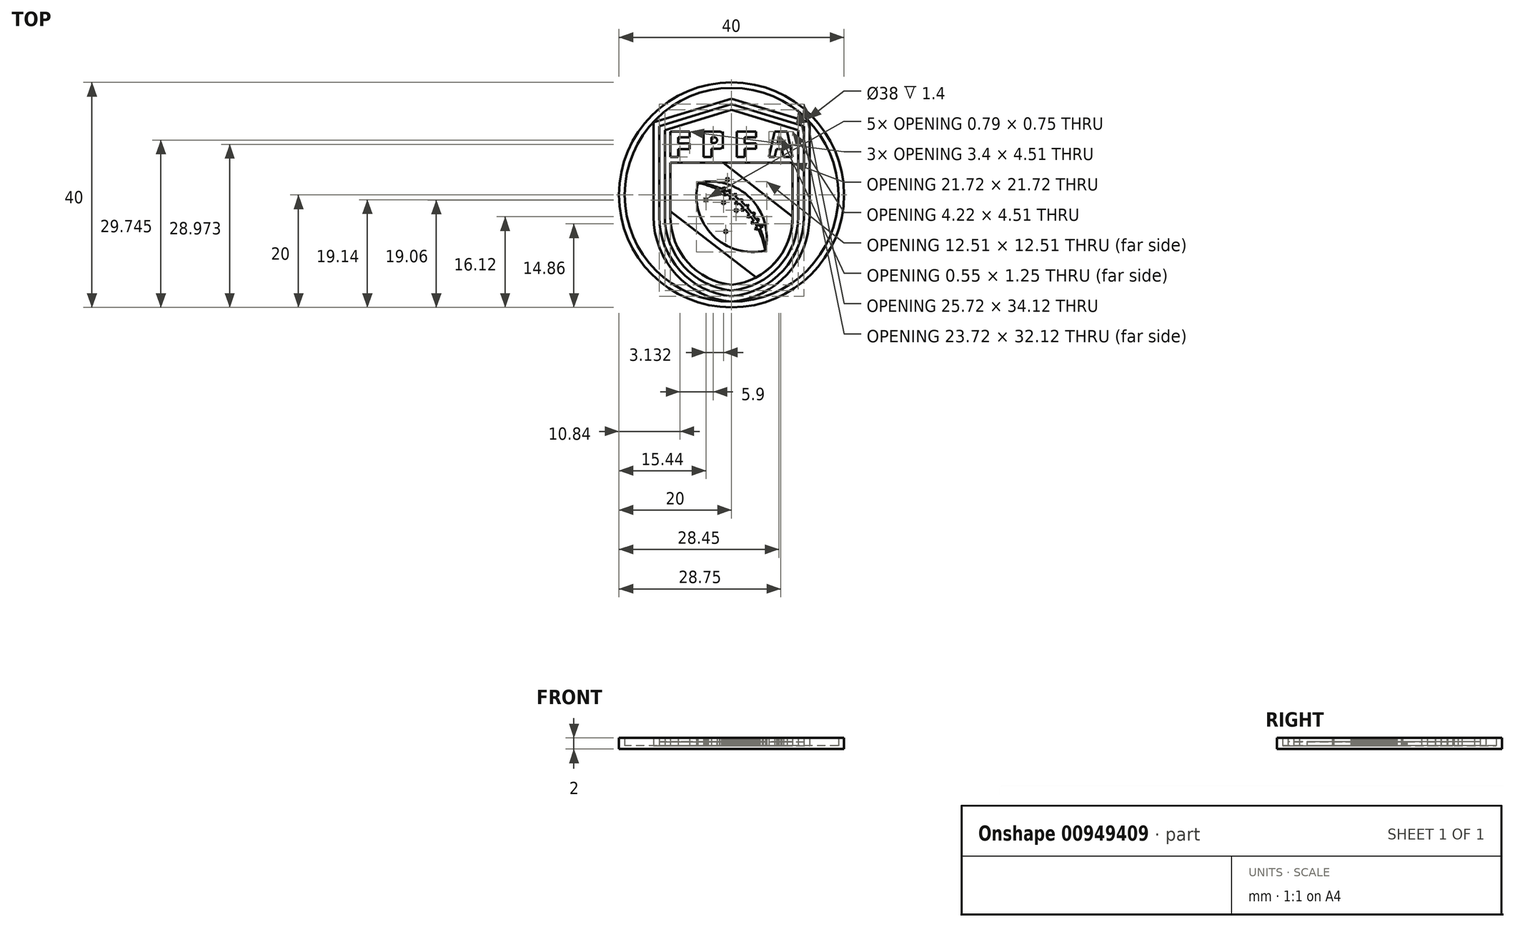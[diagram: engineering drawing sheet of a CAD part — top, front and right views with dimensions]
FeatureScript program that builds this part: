
annotation { "Feature Type Name" : "Feature", "Feature Type Description" : "" }
export const myFeature = defineFeature(function(context is Context, id is Id, definition is map)
    precondition{}
    {
        {
            var Q0;
            Q0=qCreatedBy(makeId("Top.planeOp"),FACE);
            var sketch = newSketch(context, id + "F0", { "sketchPlane" : qUnion([Q0])});
            skCircle(sketch, "E0", {"center": v(0, 0) * mm, "radius": 20 * mm});
            skSolve(sketch);
        }
        {
            var Q0;
            Q0=makeQuery(id+"F0.imprint","IMPRINT",FACE,{"disambiguationData":[TD([[makeQuery(id+"F0.imprint","IMPRINT",EDGE,{"derivedFrom":sQuery(id+"F0.wireOp",EDGE,"E0")}),1.0]])]});
            extrude(context, id + "F1", {"entities" : qUnion([Q0]), "oppositeDirection" : true, "depth" : 0.6 * mm, "offsetDistance" : 25 * mm});
        }
        {
            var Q0;
            Q0=qCreatedBy(makeId("Top.planeOp"),FACE);
            var sketch = newSketch(context, id + "F2", { "sketchPlane" : qUnion([Q0])});
            skCircle(sketch, "E1", {"center": v(0, 0) * mm, "radius": 20 * mm});
            skCircle(sketch, "E2", {"center": v(0, 0) * mm, "radius": 19 * mm});
            skSolve(sketch);
        }
        {
            var Q0;
            Q0=makeQuery(id+"F2.imprint","IMPRINT",FACE,{"disambiguationData":[TD([[makeQuery(id+"F2.imprint","IMPRINT",EDGE,{"derivedFrom":sQuery(id+"F2.wireOp",EDGE,"E1")}),1.0]])]});
            extrude(context, id + "F3", {"entities" : qUnion([Q0]), "operationType" : NewBodyOperationType.ADD, "depth" : 1.4 * mm, "offsetDistance" : 25 * mm});
        }
        {
            var Q0;
            Q0=makeQuery(id+"F1.opExtrude","CAP_FACE",FACE,{"disambiguationData":[OSD([sQuery(id+"F0.wireOp",EDGE,"E0")])],"isStart":true});
            var sketch = newSketch(context, id + "F4", { "sketchPlane" : qUnion([Q0])});
            skLineSegment(sketch, "E3", {"start": v(0, -19) * mm, "end": v(0, -3.88) * mm, "construction": true});
            skLineSegment(sketch, "E4", {"start": v(0, -3.88) * mm, "end": v(13.86, -3.88) * mm, "construction": true});
            skLineSegment(sketch, "E5", {"start": v(0, -3.88) * mm, "end": v(-13.86, -3.88) * mm, "construction": true});
            skLineSegment(sketch, "E6", {"start": v(0, -3.88) * mm, "end": v(0, 12.92) * mm, "construction": true});
            skLineSegment(sketch, "E7", {"start": v(0, 12.92) * mm, "end": v(0, 17.12) * mm, "construction": true});
            skLineSegment(sketch, "E8", {"start": v(0, 17.12) * mm, "end": v(0, 19) * mm, "construction": true});
            skLineSegment(sketch, "E9", {"start": v(0, 12.92) * mm, "end": v(13.86, 12.92) * mm, "construction": true});
            skLineSegment(sketch, "E10", {"start": v(0, 12.92) * mm, "end": v(-13.86, 12.92) * mm, "construction": true});
            skLineSegment(sketch, "E11", {"start": v(0, 17.12) * mm, "end": v(-13.86, 12.92) * mm});
            skLineSegment(sketch, "E12", {"start": v(-13.86, 12.92) * mm, "end": v(-13.86, -3.88) * mm});
            skLineSegment(sketch, "E13", {"start": v(0, 17.12) * mm, "end": v(13.86, 12.92) * mm});
            skLineSegment(sketch, "E14", {"start": v(13.86, 12.92) * mm, "end": v(13.86, -3.88) * mm});
            skArc(sketch, "E15", {"start": v(-13.86, -3.88) * mm, "mid": v(-9.87, -14.14) * mm, "end": v(0, -19) * mm});
            skArc(sketch, "E16", {"start": v(0, -19) * mm, "mid": v(9.87, -14.14) * mm, "end": v(13.86, -3.88) * mm});
            skLineSegment(sketch, "E17", {"start": v(0, 17.12) * mm, "end": v(0, 16.12) * mm, "construction": true});
            skLineSegment(sketch, "E18", {"start": v(0, 16.12) * mm, "end": v(-12.86, 12.22) * mm});
            skLineSegment(sketch, "E19", {"start": v(0, 16.12) * mm, "end": v(12.86, 12.22) * mm});
            skLineSegment(sketch, "E20", {"start": v(12.86, 12.22) * mm, "end": v(12.86, -3.88) * mm});
            skLineSegment(sketch, "E21", {"start": v(-12.86, 12.22) * mm, "end": v(-12.86, -3.88) * mm});
            skLineSegment(sketch, "E22", {"start": v(0, -19) * mm, "end": v(0, -18) * mm, "construction": true});
            skArc(sketch, "E23", {"start": v(0, -18) * mm, "mid": v(9.16, -13.43) * mm, "end": v(12.86, -3.88) * mm});
            skArc(sketch, "E24", {"start": v(-12.86, -3.88) * mm, "mid": v(-9.16, -13.43) * mm, "end": v(0, -18) * mm});
            skLineSegment(sketch, "E25", {"start": v(0, 16.12) * mm, "end": v(0, 15.12) * mm, "construction": true});
            skLineSegment(sketch, "E26", {"start": v(0, 15.12) * mm, "end": v(11.86, 11.53) * mm});
            skLineSegment(sketch, "E27", {"start": v(11.86, 11.53) * mm, "end": v(11.86, -3.88) * mm});
            skLineSegment(sketch, "E28", {"start": v(0, 15.12) * mm, "end": v(-11.86, 11.53) * mm});
            skLineSegment(sketch, "E29", {"start": v(-11.86, 11.53) * mm, "end": v(-11.86, -3.88) * mm});
            skLineSegment(sketch, "E30", {"start": v(0, -18) * mm, "end": v(0, -17) * mm, "construction": true});
            skArc(sketch, "E31", {"start": v(0, -17) * mm, "mid": v(8.46, -12.72) * mm, "end": v(11.86, -3.88) * mm});
            skArc(sketch, "E32", {"start": v(-11.86, -3.88) * mm, "mid": v(-8.46, -12.72) * mm, "end": v(0, -17) * mm});
            skLineSegment(sketch, "E33", {"start": v(0, -17) * mm, "end": v(0, -16) * mm, "construction": true});
            skLineSegment(sketch, "E34", {"start": v(-10.86, 5.72) * mm, "end": v(-10.86, -3.88) * mm});
            skLineSegment(sketch, "E35", {"start": v(10.86, 5.72) * mm, "end": v(10.86, -3.88) * mm});
            skArc(sketch, "E36", {"start": v(-10.86, -3.88) * mm, "mid": v(-7.75, -12.02) * mm, "end": v(0, -16) * mm});
            skArc(sketch, "E37", {"start": v(0, -16) * mm, "mid": v(7.75, -12.02) * mm, "end": v(10.86, -3.88) * mm});
            skLineSegment(sketch, "E38", {"start": v(0, -3.88) * mm, "end": v(0, 5.72) * mm, "construction": true});
            skLineSegment(sketch, "E39", {"start": v(-10.86, 5.72) * mm, "end": v(10.86, 5.72) * mm});
            skLineSegment(sketch, "E40", {"start": v(10.86, -3.88) * mm, "end": v(-1.5, 5.72) * mm});
            skLineSegment(sketch, "E41", {"start": v(-10.86, -2.88) * mm, "end": v(4.33, -14.68) * mm});
            skLineSegment(sketch, "E42", {"start": v(-10.86, 5.72) * mm, "end": v(-10.86, 6.72) * mm, "construction": true});
            skLineSegment(sketch, "E43", {"start": v(-10.86, 6.72) * mm, "end": v(-10.86, 11.23) * mm, "construction": true});
            skLineSegment(sketch, "E44", {"start": v(-10.86, 11.23) * mm, "end": v(10.86, 11.23) * mm, "construction": true});
            skLineSegment(sketch, "E45", {"start": v(-10.86, 6.72) * mm, "end": v(10.86, 6.72) * mm, "construction": true});
            skLineSegment(sketch, "E46", {"start": v(10.86, 5.72) * mm, "end": v(10.86, 6.72) * mm, "construction": true});
            skLineSegment(sketch, "E47", {"start": v(10.86, 6.72) * mm, "end": v(10.86, 11.23) * mm, "construction": true});
            skLineSegment(sketch, "E48", {"start": v(-10.86, 6.72) * mm, "end": v(-10.86, 11.23) * mm});
            skLineSegment(sketch, "E49", {"start": v(-10.86, 11.23) * mm, "end": v(-7.46, 11.23) * mm});
            skLineSegment(sketch, "E50", {"start": v(-7.46, 11.23) * mm, "end": v(-7.46, 10.23) * mm});
            skLineSegment(sketch, "E51", {"start": v(-7.46, 10.23) * mm, "end": v(-9.46, 10.23) * mm});
            skLineSegment(sketch, "E52", {"start": v(-9.46, 10.23) * mm, "end": v(-9.46, 9.16) * mm});
            skLineSegment(sketch, "E53", {"start": v(-9.46, 9.16) * mm, "end": v(-7.46, 9.16) * mm});
            skLineSegment(sketch, "E54", {"start": v(-7.46, 9.16) * mm, "end": v(-7.46, 8.16) * mm});
            skLineSegment(sketch, "E55", {"start": v(-7.46, 8.16) * mm, "end": v(-9.46, 8.16) * mm});
            skLineSegment(sketch, "E56", {"start": v(-9.46, 8.16) * mm, "end": v(-9.46, 6.72) * mm});
            skLineSegment(sketch, "E57", {"start": v(-9.46, 6.72) * mm, "end": v(-10.86, 6.72) * mm});
            skLineSegment(sketch, "E58", {"start": v(-4.96, 6.72) * mm, "end": v(-4.96, 11.23) * mm});
            skLineSegment(sketch, "E59", {"start": v(-4.96, 11.23) * mm, "end": v(-1.56, 11.23) * mm});
            skLineSegment(sketch, "E60", {"start": v(-3.56, 6.72) * mm, "end": v(-4.96, 6.72) * mm});
            skLineSegment(sketch, "E61", {"start": v(-3.56, 9.23) * mm, "end": v(-3.56, 10.23) * mm});
            skLineSegment(sketch, "E62", {"start": v(-3.56, 10.23) * mm, "end": v(-2.56, 10.23) * mm});
            skLineSegment(sketch, "E63", {"start": v(-2.56, 10.23) * mm, "end": v(-2.56, 9.23) * mm});
            skLineSegment(sketch, "E64", {"start": v(-2.56, 9.23) * mm, "end": v(-3.56, 9.23) * mm});
            skLineSegment(sketch, "E65", {"start": v(-1.56, 11.23) * mm, "end": v(-1.56, 8.23) * mm});
            skLineSegment(sketch, "E66", {"start": v(-1.56, 8.23) * mm, "end": v(-3.56, 8.23) * mm});
            skLineSegment(sketch, "E67", {"start": v(-3.56, 8.23) * mm, "end": v(-3.56, 6.72) * mm});
            skLineSegment(sketch, "E68", {"start": v(-1.56, 11.23) * mm, "end": v(0.94, 11.23) * mm, "construction": true});
            skLineSegment(sketch, "E69", {"start": v(0.94, 11.23) * mm, "end": v(0.94, 6.72) * mm});
            skLineSegment(sketch, "E70", {"start": v(0.94, 11.23) * mm, "end": v(2.34, 11.23) * mm});
            skLineSegment(sketch, "E71", {"start": v(2.34, 11.23) * mm, "end": v(4.34, 11.23) * mm});
            skLineSegment(sketch, "E72", {"start": v(4.34, 11.23) * mm, "end": v(4.34, 10.23) * mm});
            skLineSegment(sketch, "E73", {"start": v(4.34, 10.23) * mm, "end": v(2.34, 10.23) * mm});
            skLineSegment(sketch, "E74", {"start": v(2.34, 10.23) * mm, "end": v(2.34, 9.16) * mm});
            skLineSegment(sketch, "E75", {"start": v(2.34, 9.16) * mm, "end": v(4.34, 9.16) * mm});
            skLineSegment(sketch, "E76", {"start": v(4.34, 9.16) * mm, "end": v(4.34, 8.23) * mm});
            skLineSegment(sketch, "E77", {"start": v(4.34, 8.23) * mm, "end": v(2.34, 8.23) * mm});
            skLineSegment(sketch, "E78", {"start": v(2.34, 8.23) * mm, "end": v(2.34, 6.72) * mm});
            skLineSegment(sketch, "E79", {"start": v(2.34, 6.72) * mm, "end": v(0.94, 6.72) * mm});
            skLineSegment(sketch, "E80", {"start": v(4.34, 11.23) * mm, "end": v(6.64, 11.23) * mm, "construction": true});
            skLineSegment(sketch, "E81", {"start": v(6.64, 11.23) * mm, "end": v(6.64, 6.72) * mm, "construction": true});
            skLineSegment(sketch, "E82", {"start": v(6.64, 6.72) * mm, "end": v(7.64, 11.23) * mm});
            skLineSegment(sketch, "E83", {"start": v(7.64, 11.23) * mm, "end": v(9.86, 11.23) * mm});
            skLineSegment(sketch, "E84", {"start": v(9.86, 11.23) * mm, "end": v(10.86, 6.72) * mm});
            skLineSegment(sketch, "E85", {"start": v(10.86, 6.72) * mm, "end": v(9.26, 6.72) * mm});
            skLineSegment(sketch, "E86", {"start": v(6.64, 6.72) * mm, "end": v(7.64, 6.72) * mm});
            skLineSegment(sketch, "E87", {"start": v(9.26, 6.72) * mm, "end": v(8.45, 10.37) * mm});
            skLineSegment(sketch, "E88", {"start": v(7.64, 6.72) * mm, "end": v(8.45, 10.37) * mm});
            skLineSegment(sketch, "E89", {"start": v(7.95, 8.12) * mm, "end": v(8.95, 8.12) * mm});
            skLineSegment(sketch, "E90", {"start": v(8.17, 9.12) * mm, "end": v(8.73, 9.12) * mm});
            skLineSegment(sketch, "E91", {"start": v(0, -3.88) * mm, "end": v(0, -9.88) * mm, "construction": true});
            skLineSegment(sketch, "E92", {"start": v(0, -9.88) * mm, "end": v(6, -9.88) * mm, "construction": true});
            skLineSegment(sketch, "E93", {"start": v(0, -3.88) * mm, "end": v(0, 2.12) * mm, "construction": true});
            skLineSegment(sketch, "E94", {"start": v(0, 2.12) * mm, "end": v(-6, 2.12) * mm, "construction": true});
            skArc(sketch, "E95", {"start": v(-6, 2.12) * mm, "mid": v(-3.33, -7.2) * mm, "end": v(6, -9.88) * mm});
            skArc(sketch, "E96", {"start": v(6, -9.88) * mm, "mid": v(3.33, -0.55) * mm, "end": v(-6, 2.12) * mm});
            skArc(sketch, "E97", {"start": v(6, -9.88) * mm, "mid": v(1.86, -2.02) * mm, "end": v(-6, 2.12) * mm});
            skArc(sketch, "E98", {"start": v(6, -9.88) * mm, "mid": v(2.23, -1.65) * mm, "end": v(-6, 2.12) * mm});
            skLineSegment(sketch, "E99", {"start": v(-2.57, 0.5) * mm, "end": v(-1.45, 1.33) * mm});
            skLineSegment(sketch, "E100", {"start": v(-1.45, 1.33) * mm, "end": v(-1.05, 1.25) * mm});
            skLineSegment(sketch, "E101", {"start": v(-1.05, 1.25) * mm, "end": v(-2.18, 0.41) * mm});
            skLineSegment(sketch, "E102", {"start": v(-2.18, 0.41) * mm, "end": v(-2.57, 0.5) * mm});
            skLineSegment(sketch, "E103", {"start": v(-1.45, 0) * mm, "end": v(-0.39, 0.9) * mm});
            skLineSegment(sketch, "E104", {"start": v(-0.39, 0.9) * mm, "end": v(0, 0.81) * mm});
            skLineSegment(sketch, "E105", {"start": v(0, 0.81) * mm, "end": v(-1.07, -0.1) * mm});
            skLineSegment(sketch, "E106", {"start": v(-1.07, -0.1) * mm, "end": v(-1.45, 0) * mm});
            skLineSegment(sketch, "E107", {"start": v(-0.4, -0.66) * mm, "end": v(0.68, 0.24) * mm});
            skLineSegment(sketch, "E108", {"start": v(0.68, 0.24) * mm, "end": v(0.94, -0.06) * mm});
            skLineSegment(sketch, "E109", {"start": v(0.94, -0.06) * mm, "end": v(-0.13, -0.96) * mm});
            skLineSegment(sketch, "E110", {"start": v(-0.13, -0.96) * mm, "end": v(-0.4, -0.66) * mm});
            skLineSegment(sketch, "E111", {"start": v(0.58, -1.54) * mm, "end": v(1.7, -0.7) * mm});
            skLineSegment(sketch, "E112", {"start": v(1.7, -0.7) * mm, "end": v(2.03, -0.93) * mm});
            skLineSegment(sketch, "E113", {"start": v(2.03, -0.93) * mm, "end": v(0.91, -1.76) * mm});
            skLineSegment(sketch, "E114", {"start": v(0.91, -1.76) * mm, "end": v(0.58, -1.54) * mm});
            skLineSegment(sketch, "E115", {"start": v(1.7, -2.56) * mm, "end": v(2.82, -1.73) * mm});
            skLineSegment(sketch, "E116", {"start": v(2.82, -1.73) * mm, "end": v(3.06, -2.05) * mm});
            skLineSegment(sketch, "E117", {"start": v(3.06, -2.05) * mm, "end": v(1.94, -2.88) * mm});
            skLineSegment(sketch, "E118", {"start": v(1.94, -2.88) * mm, "end": v(1.7, -2.56) * mm});
            skLineSegment(sketch, "E119", {"start": v(2.76, -3.75) * mm, "end": v(4, -3.1) * mm});
            skLineSegment(sketch, "E120", {"start": v(4, -3.1) * mm, "end": v(4.23, -3.43) * mm});
            skLineSegment(sketch, "E121", {"start": v(4.23, -3.43) * mm, "end": v(2.99, -4.07) * mm});
            skLineSegment(sketch, "E122", {"start": v(2.99, -4.07) * mm, "end": v(2.76, -3.75) * mm});
            skLineSegment(sketch, "E123", {"start": v(3.47, -4.85) * mm, "end": v(4.7, -4.2) * mm});
            skLineSegment(sketch, "E124", {"start": v(4.7, -4.2) * mm, "end": v(4.94, -4.51) * mm});
            skLineSegment(sketch, "E125", {"start": v(4.94, -4.51) * mm, "end": v(3.7, -5.17) * mm});
            skLineSegment(sketch, "E126", {"start": v(3.7, -5.17) * mm, "end": v(3.47, -4.85) * mm});
            skLineSegment(sketch, "E127", {"start": v(4.18, -5.88) * mm, "end": v(5.42, -5.24) * mm});
            skLineSegment(sketch, "E128", {"start": v(5.42, -5.24) * mm, "end": v(5.6, -5.6) * mm});
            skLineSegment(sketch, "E129", {"start": v(5.6, -5.6) * mm, "end": v(4.36, -6.24) * mm});
            skLineSegment(sketch, "E130", {"start": v(4.36, -6.24) * mm, "end": v(4.18, -5.88) * mm});
            skLineSegment(sketch, "E131", {"start": v(-1.12, 2.84) * mm, "end": v(-0.82, 2.84) * mm});
            skLineSegment(sketch, "E132", {"start": v(-0.82, 2.84) * mm, "end": v(-0.73, 3.13) * mm});
            skLineSegment(sketch, "E133", {"start": v(-0.73, 3.13) * mm, "end": v(-0.64, 2.84) * mm});
            skLineSegment(sketch, "E134", {"start": v(-0.64, 2.84) * mm, "end": v(-0.34, 2.84) * mm});
            skLineSegment(sketch, "E135", {"start": v(-0.34, 2.84) * mm, "end": v(-0.58, 2.66) * mm});
            skLineSegment(sketch, "E136", {"start": v(-0.64, 2.84) * mm, "end": v(-0.58, 2.66) * mm, "construction": true});
            skLineSegment(sketch, "E137", {"start": v(-0.58, 2.66) * mm, "end": v(-0.49, 2.38) * mm});
            skLineSegment(sketch, "E138", {"start": v(-1.12, 2.84) * mm, "end": v(-0.88, 2.66) * mm});
            skLineSegment(sketch, "E139", {"start": v(-0.88, 2.66) * mm, "end": v(-0.82, 2.84) * mm, "construction": true});
            skLineSegment(sketch, "E140", {"start": v(-0.88, 2.66) * mm, "end": v(-0.97, 2.38) * mm});
            skLineSegment(sketch, "E141", {"start": v(-0.97, 2.38) * mm, "end": v(-0.73, 2.56) * mm});
            skLineSegment(sketch, "E142", {"start": v(-0.73, 2.56) * mm, "end": v(-0.49, 2.38) * mm});
            skLineSegment(sketch, "E143", {"start": v(-0.73, 2.56) * mm, "end": v(-0.88, 2.66) * mm, "construction": true});
            skLineSegment(sketch, "E144.1.0.0", {"start": v(-4.8, -1.23) * mm, "end": v(-4.56, -1.06) * mm});
            skLineSegment(sketch, "E144.1.0.1", {"start": v(-4.71, -0.95) * mm, "end": v(-4.8, -1.23) * mm});
            skLineSegment(sketch, "E144.1.0.2", {"start": v(-4.56, -0.49) * mm, "end": v(-4.47, -0.77) * mm});
            skLineSegment(sketch, "E144.1.0.3", {"start": v(-4.65, -0.77) * mm, "end": v(-4.56, -0.49) * mm});
            skLineSegment(sketch, "E144.1.0.4", {"start": v(-4.56, -1.06) * mm, "end": v(-4.71, -0.95) * mm, "construction": true});
            skLineSegment(sketch, "E144.1.0.5", {"start": v(-4.95, -0.77) * mm, "end": v(-4.65, -0.77) * mm});
            skLineSegment(sketch, "E144.1.0.6", {"start": v(-4.47, -0.77) * mm, "end": v(-4.17, -0.77) * mm});
            skLineSegment(sketch, "E144.1.0.7", {"start": v(-4.17, -0.77) * mm, "end": v(-4.41, -0.95) * mm});
            skLineSegment(sketch, "E144.1.0.8", {"start": v(-4.95, -0.77) * mm, "end": v(-4.71, -0.95) * mm});
            skLineSegment(sketch, "E144.1.0.9", {"start": v(-4.47, -0.77) * mm, "end": v(-4.41, -0.95) * mm, "construction": true});
            skLineSegment(sketch, "E144.1.0.10", {"start": v(-4.56, -1.06) * mm, "end": v(-4.32, -1.23) * mm});
            skLineSegment(sketch, "E144.1.0.11", {"start": v(-4.41, -0.95) * mm, "end": v(-4.32, -1.23) * mm});
            skLineSegment(sketch, "E144.1.0.12", {"start": v(-4.71, -0.95) * mm, "end": v(-4.65, -0.77) * mm, "construction": true});
            skLineSegment(sketch, "E144.2.0.0", {"start": v(-1.67, -1.7) * mm, "end": v(-1.43, -1.51) * mm});
            skLineSegment(sketch, "E144.2.0.1", {"start": v(-1.58, -1.4) * mm, "end": v(-1.67, -1.7) * mm});
            skLineSegment(sketch, "E144.2.0.2", {"start": v(-1.43, -0.94) * mm, "end": v(-1.34, -1.23) * mm});
            skLineSegment(sketch, "E144.2.0.3", {"start": v(-1.52, -1.23) * mm, "end": v(-1.43, -0.94) * mm});
            skLineSegment(sketch, "E144.2.0.4", {"start": v(-1.43, -1.51) * mm, "end": v(-1.58, -1.4) * mm, "construction": true});
            skLineSegment(sketch, "E144.2.0.5", {"start": v(-1.82, -1.23) * mm, "end": v(-1.52, -1.23) * mm});
            skLineSegment(sketch, "E144.2.0.6", {"start": v(-1.34, -1.23) * mm, "end": v(-1.04, -1.23) * mm});
            skLineSegment(sketch, "E144.2.0.7", {"start": v(-1.04, -1.23) * mm, "end": v(-1.28, -1.4) * mm});
            skLineSegment(sketch, "E144.2.0.8", {"start": v(-1.82, -1.23) * mm, "end": v(-1.58, -1.4) * mm});
            skLineSegment(sketch, "E144.2.0.9", {"start": v(-1.34, -1.23) * mm, "end": v(-1.28, -1.4) * mm, "construction": true});
            skLineSegment(sketch, "E144.2.0.10", {"start": v(-1.43, -1.51) * mm, "end": v(-1.19, -1.7) * mm});
            skLineSegment(sketch, "E144.2.0.11", {"start": v(-1.28, -1.4) * mm, "end": v(-1.19, -1.7) * mm});
            skLineSegment(sketch, "E144.2.0.12", {"start": v(-1.58, -1.4) * mm, "end": v(-1.52, -1.23) * mm, "construction": true});
            skPoint(sketch, "E145", {"position": v(-4.56, -0.49) * mm});
            skPoint(sketch, "E146", {"position": v(-1.43, -0.94) * mm});
            skPoint(sketch, "E147", {"position": v(0.83, -2.37) * mm});
            skPoint(sketch, "E148", {"position": v(-1.03, -6.1) * mm});
            skLineSegment(sketch, "E149.1.0.0", {"start": v(1.22, -2.66) * mm, "end": v(0.98, -2.83) * mm});
            skLineSegment(sketch, "E149.1.0.1", {"start": v(0.44, -2.66) * mm, "end": v(0.74, -2.66) * mm});
            skLineSegment(sketch, "E149.1.0.2", {"start": v(0.68, -2.83) * mm, "end": v(0.74, -2.66) * mm, "construction": true});
            skLineSegment(sketch, "E149.1.0.3", {"start": v(0.83, -2.94) * mm, "end": v(1.07, -3.12) * mm});
            skLineSegment(sketch, "E149.1.0.4", {"start": v(0.83, -2.37) * mm, "end": v(0.92, -2.66) * mm});
            skLineSegment(sketch, "E149.1.0.5", {"start": v(0.68, -2.83) * mm, "end": v(0.59, -3.12) * mm});
            skLineSegment(sketch, "E149.1.0.6", {"start": v(0.98, -2.83) * mm, "end": v(1.07, -3.12) * mm});
            skLineSegment(sketch, "E149.1.0.7", {"start": v(0.83, -2.94) * mm, "end": v(0.68, -2.83) * mm, "construction": true});
            skLineSegment(sketch, "E149.1.0.8", {"start": v(0.44, -2.66) * mm, "end": v(0.68, -2.83) * mm});
            skLineSegment(sketch, "E149.1.0.9", {"start": v(0.92, -2.66) * mm, "end": v(0.98, -2.83) * mm, "construction": true});
            skLineSegment(sketch, "E149.1.0.10", {"start": v(0.92, -2.66) * mm, "end": v(1.22, -2.66) * mm});
            skLineSegment(sketch, "E149.1.0.11", {"start": v(0.59, -3.12) * mm, "end": v(0.83, -2.94) * mm});
            skLineSegment(sketch, "E149.1.0.12", {"start": v(0.74, -2.66) * mm, "end": v(0.83, -2.37) * mm});
            skLineSegment(sketch, "E149.2.0.0", {"start": v(-0.64, -6.39) * mm, "end": v(-0.88, -6.57) * mm});
            skLineSegment(sketch, "E149.2.0.1", {"start": v(-1.42, -6.39) * mm, "end": v(-1.12, -6.39) * mm});
            skLineSegment(sketch, "E149.2.0.2", {"start": v(-1.18, -6.57) * mm, "end": v(-1.12, -6.39) * mm, "construction": true});
            skLineSegment(sketch, "E149.2.0.3", {"start": v(-1.03, -6.67) * mm, "end": v(-0.79, -6.85) * mm});
            skLineSegment(sketch, "E149.2.0.4", {"start": v(-1.03, -6.1) * mm, "end": v(-0.94, -6.39) * mm});
            skLineSegment(sketch, "E149.2.0.5", {"start": v(-1.18, -6.57) * mm, "end": v(-1.27, -6.85) * mm});
            skLineSegment(sketch, "E149.2.0.6", {"start": v(-0.88, -6.57) * mm, "end": v(-0.79, -6.85) * mm});
            skLineSegment(sketch, "E149.2.0.7", {"start": v(-1.03, -6.67) * mm, "end": v(-1.18, -6.57) * mm, "construction": true});
            skLineSegment(sketch, "E149.2.0.8", {"start": v(-1.42, -6.39) * mm, "end": v(-1.18, -6.57) * mm});
            skLineSegment(sketch, "E149.2.0.9", {"start": v(-0.94, -6.39) * mm, "end": v(-0.88, -6.57) * mm, "construction": true});
            skLineSegment(sketch, "E149.2.0.10", {"start": v(-0.94, -6.39) * mm, "end": v(-0.64, -6.39) * mm});
            skLineSegment(sketch, "E149.2.0.11", {"start": v(-1.27, -6.85) * mm, "end": v(-1.03, -6.67) * mm});
            skLineSegment(sketch, "E149.2.0.12", {"start": v(-1.12, -6.39) * mm, "end": v(-1.03, -6.1) * mm});
            skSolve(sketch);
        }
        {
            var Q0;
            Q0=makeQuery(id+"F4.imprint","IMPRINT",FACE,{"disambiguationData":[TD([[makeQuery(id+"F4.imprint","IMPRINT",EDGE,{"derivedFrom":sQuery(id+"F4.wireOp",EDGE,"E11")}),1.0]])]});
            var Q1;
            Q1=makeQuery(id+"F4.imprint","IMPRINT",FACE,{"disambiguationData":[TD([[makeQuery(id+"F4.imprint","IMPRINT",EDGE,{"derivedFrom":sQuery(id+"F4.wireOp",EDGE,"E26")}),-1.0]])]});
            var Q2;
            Q2=makeQuery(id+"F4.imprint","IMPRINT",FACE,{"disambiguationData":[TD([[makeQuery(id+"F4.imprint","IMPRINT",EDGE,{"derivedFrom":sQuery(id+"F4.wireOp",EDGE,"E61")}),-1.0]])]});
            var Q3;
            {var subQ0=sQuery(id+"F4.wireOp",EDGE,"E90");Q3=makeQuery(id+"F4.imprint","IMPRINT",FACE,{"disambiguationData":[TD([[makeQuery(id+"F4.imprint","IMPRINT",EDGE,{"derivedFrom":subQ0}),1.0]])]});}
            extrude(context, id + "F5", {"entities" : qUnion([Q0, Q1, Q2, Q3]), "depth" : 1.4 * mm, "offsetDistance" : 25 * mm});
        }
        {
            var Q0;
            {var subQ0=sQuery(id+"F4.wireOp",EDGE,"E40");Q0=makeQuery(id+"F4.imprint","IMPRINT",FACE,{"disambiguationData":[TD([[makeQuery(id+"F4.imprint","IMPRINT",EDGE,{"derivedFrom":subQ0}),1.0]])]});}
            var Q1;
            {var subQ0=sQuery(id+"F4.wireOp",EDGE,"E115");var subQ1=sQuery(id+"F4.wireOp",EDGE,"E97");var subQ2=makeQuery(id+"F4.imprint","INTERSECT",VERTEX,{"derivedFrom":[subQ1,subQ0]});Q1=makeQuery(id+"F4.imprint","IMPRINT",FACE,{"disambiguationData":[TD([[makeQuery(id+"F4.imprint","IMPRINT",EDGE,{"disambiguationData":[TD([[subQ2,-1.0]])],"derivedFrom":subQ1}),-1.0]])]});}
            var Q2;
            {var subQ0=sQuery(id+"F4.wireOp",EDGE,"E98");var subQ3=sQuery(id+"F4.wireOp",EDGE,"E99");var subQ5=makeQuery(id+"F4.imprint","INTERSECT",VERTEX,{"derivedFrom":[subQ0,subQ3]});Q2=makeQuery(id+"F4.imprint","IMPRINT",FACE,{"disambiguationData":[TD([[makeQuery(id+"F4.imprint","IMPRINT",EDGE,{"disambiguationData":[TD([[subQ5,1.0]])],"derivedFrom":subQ3}),1.0]])]});}
            var Q3;
            {var subQ5=sQuery(id+"F4.wireOp",EDGE,"E100");Q3=makeQuery(id+"F4.imprint","IMPRINT",FACE,{"disambiguationData":[TD([[makeQuery(id+"F4.imprint","IMPRINT",EDGE,{"derivedFrom":subQ5}),-1.0]])]});}
            var Q4;
            {var subQ0=sQuery(id+"F4.wireOp",EDGE,"E101");var subQ1=sQuery(id+"F4.wireOp",EDGE,"E97");var subQ2=makeQuery(id+"F4.imprint","INTERSECT",VERTEX,{"derivedFrom":[subQ1,subQ0]});Q4=makeQuery(id+"F4.imprint","IMPRINT",FACE,{"disambiguationData":[TD([[makeQuery(id+"F4.imprint","IMPRINT",EDGE,{"disambiguationData":[TD([[subQ2,-1.0]])],"derivedFrom":subQ1}),-1.0]])]});}
            var Q5;
            {var subQ5=sQuery(id+"F4.wireOp",EDGE,"E102");Q5=makeQuery(id+"F4.imprint","IMPRINT",FACE,{"disambiguationData":[TD([[makeQuery(id+"F4.imprint","IMPRINT",EDGE,{"derivedFrom":subQ5}),-1.0]])]});}
            var Q6;
            {var subQ0=sQuery(id+"F4.wireOp",EDGE,"E101");var subQ1=sQuery(id+"F4.wireOp",EDGE,"E97");var subQ2=makeQuery(id+"F4.imprint","INTERSECT",VERTEX,{"derivedFrom":[subQ1,subQ0]});Q6=makeQuery(id+"F4.imprint","IMPRINT",FACE,{"disambiguationData":[TD([[makeQuery(id+"F4.imprint","IMPRINT",EDGE,{"disambiguationData":[TD([[subQ2,1.0]])],"derivedFrom":subQ1}),-1.0]])]});}
            var Q7;
            {var subQ0=sQuery(id+"F4.wireOp",EDGE,"E103");var subQ1=sQuery(id+"F4.wireOp",EDGE,"E97");var subQ2=makeQuery(id+"F4.imprint","INTERSECT",VERTEX,{"derivedFrom":[subQ1,subQ0]});Q7=makeQuery(id+"F4.imprint","IMPRINT",FACE,{"disambiguationData":[TD([[makeQuery(id+"F4.imprint","IMPRINT",EDGE,{"disambiguationData":[TD([[subQ2,1.0]])],"derivedFrom":subQ1}),-1.0]])]});}
            var Q8;
            {var subQ5=sQuery(id+"F4.wireOp",EDGE,"E106");Q8=makeQuery(id+"F4.imprint","IMPRINT",FACE,{"disambiguationData":[TD([[makeQuery(id+"F4.imprint","IMPRINT",EDGE,{"derivedFrom":subQ5}),-1.0]])]});}
            var Q9;
            {var subQ5=sQuery(id+"F4.wireOp",EDGE,"E104");Q9=makeQuery(id+"F4.imprint","IMPRINT",FACE,{"disambiguationData":[TD([[makeQuery(id+"F4.imprint","IMPRINT",EDGE,{"derivedFrom":subQ5}),-1.0]])]});}
            var Q10;
            {var subQ0=sQuery(id+"F4.wireOp",EDGE,"E107");var subQ1=sQuery(id+"F4.wireOp",EDGE,"E97");var subQ2=makeQuery(id+"F4.imprint","INTERSECT",VERTEX,{"derivedFrom":[subQ1,subQ0]});Q10=makeQuery(id+"F4.imprint","IMPRINT",FACE,{"disambiguationData":[TD([[makeQuery(id+"F4.imprint","IMPRINT",EDGE,{"disambiguationData":[TD([[subQ2,-1.0]])],"derivedFrom":subQ1}),-1.0]])]});}
            var Q11;
            {var subQ5=sQuery(id+"F4.wireOp",EDGE,"E110");Q11=makeQuery(id+"F4.imprint","IMPRINT",FACE,{"disambiguationData":[TD([[makeQuery(id+"F4.imprint","IMPRINT",EDGE,{"derivedFrom":subQ5}),-1.0]])]});}
            var Q12;
            {var subQ0=sQuery(id+"F4.wireOp",EDGE,"E107");var subQ1=sQuery(id+"F4.wireOp",EDGE,"E97");var subQ2=makeQuery(id+"F4.imprint","INTERSECT",VERTEX,{"derivedFrom":[subQ1,subQ0]});Q12=makeQuery(id+"F4.imprint","IMPRINT",FACE,{"disambiguationData":[TD([[makeQuery(id+"F4.imprint","IMPRINT",EDGE,{"disambiguationData":[TD([[subQ2,1.0]])],"derivedFrom":subQ1}),-1.0]])]});}
            var Q13;
            {var subQ5=sQuery(id+"F4.wireOp",EDGE,"E108");Q13=makeQuery(id+"F4.imprint","IMPRINT",FACE,{"disambiguationData":[TD([[makeQuery(id+"F4.imprint","IMPRINT",EDGE,{"derivedFrom":subQ5}),-1.0]])]});}
            var Q14;
            {var subQ0=sQuery(id+"F4.wireOp",EDGE,"E109");var subQ1=sQuery(id+"F4.wireOp",EDGE,"E97");var subQ2=makeQuery(id+"F4.imprint","INTERSECT",VERTEX,{"derivedFrom":[subQ1,subQ0]});Q14=makeQuery(id+"F4.imprint","IMPRINT",FACE,{"disambiguationData":[TD([[makeQuery(id+"F4.imprint","IMPRINT",EDGE,{"disambiguationData":[TD([[subQ2,1.0]])],"derivedFrom":subQ1}),-1.0]])]});}
            var Q15;
            {var subQ5=sQuery(id+"F4.wireOp",EDGE,"E112");Q15=makeQuery(id+"F4.imprint","IMPRINT",FACE,{"disambiguationData":[TD([[makeQuery(id+"F4.imprint","IMPRINT",EDGE,{"derivedFrom":subQ5}),-1.0]])]});}
            var Q16;
            {var subQ0=sQuery(id+"F4.wireOp",EDGE,"E113");var subQ1=sQuery(id+"F4.wireOp",EDGE,"E97");var subQ2=makeQuery(id+"F4.imprint","INTERSECT",VERTEX,{"derivedFrom":[subQ1,subQ0]});Q16=makeQuery(id+"F4.imprint","IMPRINT",FACE,{"disambiguationData":[TD([[makeQuery(id+"F4.imprint","IMPRINT",EDGE,{"disambiguationData":[TD([[subQ2,-1.0]])],"derivedFrom":subQ1}),-1.0]])]});}
            var Q17;
            {var subQ5=sQuery(id+"F4.wireOp",EDGE,"E114");Q17=makeQuery(id+"F4.imprint","IMPRINT",FACE,{"disambiguationData":[TD([[makeQuery(id+"F4.imprint","IMPRINT",EDGE,{"derivedFrom":subQ5}),-1.0]])]});}
            var Q18;
            {var subQ5=sQuery(id+"F4.wireOp",EDGE,"E116");Q18=makeQuery(id+"F4.imprint","IMPRINT",FACE,{"disambiguationData":[TD([[makeQuery(id+"F4.imprint","IMPRINT",EDGE,{"derivedFrom":subQ5}),-1.0]])]});}
            var Q19;
            {var subQ0=sQuery(id+"F4.wireOp",EDGE,"E115");var subQ1=sQuery(id+"F4.wireOp",EDGE,"E97");var subQ2=makeQuery(id+"F4.imprint","INTERSECT",VERTEX,{"derivedFrom":[subQ1,subQ0]});Q19=makeQuery(id+"F4.imprint","IMPRINT",FACE,{"disambiguationData":[TD([[makeQuery(id+"F4.imprint","IMPRINT",EDGE,{"disambiguationData":[TD([[subQ2,1.0]])],"derivedFrom":subQ1}),-1.0]])]});}
            var Q20;
            {var subQ5=sQuery(id+"F4.wireOp",EDGE,"E118");Q20=makeQuery(id+"F4.imprint","IMPRINT",FACE,{"disambiguationData":[TD([[makeQuery(id+"F4.imprint","IMPRINT",EDGE,{"derivedFrom":subQ5}),-1.0]])]});}
            var Q21;
            {var subQ0=sQuery(id+"F4.wireOp",EDGE,"E117");var subQ1=sQuery(id+"F4.wireOp",EDGE,"E97");var subQ2=makeQuery(id+"F4.imprint","INTERSECT",VERTEX,{"derivedFrom":[subQ1,subQ0]});Q21=makeQuery(id+"F4.imprint","IMPRINT",FACE,{"disambiguationData":[TD([[makeQuery(id+"F4.imprint","IMPRINT",EDGE,{"disambiguationData":[TD([[subQ2,1.0]])],"derivedFrom":subQ1}),-1.0]])]});}
            var Q22;
            {var subQ0=sQuery(id+"F4.wireOp",EDGE,"E119");var subQ1=sQuery(id+"F4.wireOp",EDGE,"E97");var subQ2=makeQuery(id+"F4.imprint","INTERSECT",VERTEX,{"derivedFrom":[subQ1,subQ0]});Q22=makeQuery(id+"F4.imprint","IMPRINT",FACE,{"disambiguationData":[TD([[makeQuery(id+"F4.imprint","IMPRINT",EDGE,{"disambiguationData":[TD([[subQ2,1.0]])],"derivedFrom":subQ1}),-1.0]])]});}
            var Q23;
            {var subQ5=sQuery(id+"F4.wireOp",EDGE,"E120");Q23=makeQuery(id+"F4.imprint","IMPRINT",FACE,{"disambiguationData":[TD([[makeQuery(id+"F4.imprint","IMPRINT",EDGE,{"derivedFrom":subQ5}),-1.0]])]});}
            var Q24;
            {var subQ5=sQuery(id+"F4.wireOp",EDGE,"E122");Q24=makeQuery(id+"F4.imprint","IMPRINT",FACE,{"disambiguationData":[TD([[makeQuery(id+"F4.imprint","IMPRINT",EDGE,{"derivedFrom":subQ5}),-1.0]])]});}
            var Q25;
            {var subQ0=sQuery(id+"F4.wireOp",EDGE,"E123");var subQ1=sQuery(id+"F4.wireOp",EDGE,"E97");var subQ2=makeQuery(id+"F4.imprint","INTERSECT",VERTEX,{"derivedFrom":[subQ1,subQ0]});Q25=makeQuery(id+"F4.imprint","IMPRINT",FACE,{"disambiguationData":[TD([[makeQuery(id+"F4.imprint","IMPRINT",EDGE,{"disambiguationData":[TD([[subQ2,-1.0]])],"derivedFrom":subQ1}),-1.0]])]});}
            var Q26;
            {var subQ0=sQuery(id+"F4.wireOp",EDGE,"E125");var subQ1=sQuery(id+"F4.wireOp",EDGE,"E97");var subQ2=makeQuery(id+"F4.imprint","INTERSECT",VERTEX,{"derivedFrom":[subQ1,subQ0]});Q26=makeQuery(id+"F4.imprint","IMPRINT",FACE,{"disambiguationData":[TD([[makeQuery(id+"F4.imprint","IMPRINT",EDGE,{"disambiguationData":[TD([[subQ2,-1.0]])],"derivedFrom":subQ1}),-1.0]])]});}
            var Q27;
            {var subQ5=sQuery(id+"F4.wireOp",EDGE,"E124");Q27=makeQuery(id+"F4.imprint","IMPRINT",FACE,{"disambiguationData":[TD([[makeQuery(id+"F4.imprint","IMPRINT",EDGE,{"derivedFrom":subQ5}),-1.0]])]});}
            var Q28;
            {var subQ5=sQuery(id+"F4.wireOp",EDGE,"E126");Q28=makeQuery(id+"F4.imprint","IMPRINT",FACE,{"disambiguationData":[TD([[makeQuery(id+"F4.imprint","IMPRINT",EDGE,{"derivedFrom":subQ5}),-1.0]])]});}
            var Q29;
            {var subQ0=sQuery(id+"F4.wireOp",EDGE,"E125");var subQ1=sQuery(id+"F4.wireOp",EDGE,"E97");var subQ2=makeQuery(id+"F4.imprint","INTERSECT",VERTEX,{"derivedFrom":[subQ1,subQ0]});Q29=makeQuery(id+"F4.imprint","IMPRINT",FACE,{"disambiguationData":[TD([[makeQuery(id+"F4.imprint","IMPRINT",EDGE,{"disambiguationData":[TD([[subQ2,1.0]])],"derivedFrom":subQ1}),-1.0]])]});}
            var Q30;
            {var subQ0=sQuery(id+"F4.wireOp",EDGE,"E129");var subQ1=sQuery(id+"F4.wireOp",EDGE,"E97");var subQ2=makeQuery(id+"F4.imprint","INTERSECT",VERTEX,{"derivedFrom":[subQ1,subQ0]});Q30=makeQuery(id+"F4.imprint","IMPRINT",FACE,{"disambiguationData":[TD([[makeQuery(id+"F4.imprint","IMPRINT",EDGE,{"disambiguationData":[TD([[subQ2,-1.0]])],"derivedFrom":subQ1}),-1.0]])]});}
            var Q31;
            {var subQ5=sQuery(id+"F4.wireOp",EDGE,"E128");Q31=makeQuery(id+"F4.imprint","IMPRINT",FACE,{"disambiguationData":[TD([[makeQuery(id+"F4.imprint","IMPRINT",EDGE,{"derivedFrom":subQ5}),-1.0]])]});}
            var Q32;
            {var subQ5=sQuery(id+"F4.wireOp",EDGE,"E130");Q32=makeQuery(id+"F4.imprint","IMPRINT",FACE,{"disambiguationData":[TD([[makeQuery(id+"F4.imprint","IMPRINT",EDGE,{"derivedFrom":subQ5}),-1.0]])]});}
            var Q33;
            {var subQ1=sQuery(id+"F4.wireOp",EDGE,"E97");var subQ3=sQuery(id+"F4.wireOp",EDGE,"E129");var subQ4=makeQuery(id+"F4.imprint","INTERSECT",VERTEX,{"derivedFrom":[subQ1,subQ3]});Q33=makeQuery(id+"F4.imprint","IMPRINT",FACE,{"disambiguationData":[TD([[makeQuery(id+"F4.imprint","IMPRINT",EDGE,{"disambiguationData":[TD([[subQ4,1.0]])],"derivedFrom":subQ3}),1.0]])]});}
            var Q34;
            Q34=makeQuery(id+"F4.imprint","IMPRINT",FACE,{"disambiguationData":[TD([[makeQuery(id+"F4.imprint","IMPRINT",EDGE,{"derivedFrom":sQuery(id+"F4.wireOp",EDGE,"E18")}),1.0]])]});
            var Q35;
            Q35=makeQuery(id+"F4.imprint","IMPRINT",FACE,{"disambiguationData":[TD([[makeQuery(id+"F4.imprint","IMPRINT",EDGE,{"derivedFrom":sQuery(id+"F4.wireOp",EDGE,"E82")}),-1.0]])]});
            var Q36;
            {var subQ2=sQuery(id+"F4.wireOp",EDGE,"E89");Q36=makeQuery(id+"F4.imprint","IMPRINT",FACE,{"disambiguationData":[TD([[makeQuery(id+"F4.imprint","IMPRINT",EDGE,{"derivedFrom":subQ2}),1.0]])]});}
            var Q37;
            Q37=makeQuery(id+"F4.imprint","IMPRINT",FACE,{"disambiguationData":[TD([[makeQuery(id+"F4.imprint","IMPRINT",EDGE,{"derivedFrom":sQuery(id+"F4.wireOp",EDGE,"E69")}),1.0]])]});
            var Q38;
            Q38=makeQuery(id+"F4.imprint","IMPRINT",FACE,{"disambiguationData":[TD([[makeQuery(id+"F4.imprint","IMPRINT",EDGE,{"derivedFrom":sQuery(id+"F4.wireOp",EDGE,"E58")}),-1.0]])]});
            var Q39;
            Q39=makeQuery(id+"F4.imprint","IMPRINT",FACE,{"disambiguationData":[TD([[makeQuery(id+"F4.imprint","IMPRINT",EDGE,{"derivedFrom":sQuery(id+"F4.wireOp",EDGE,"E48")}),-1.0]])]});
            extrude(context, id + "F6", {"entities" : qUnion([Q0, Q1, Q2, Q3, Q4, Q5, Q6, Q7, Q8, Q9, Q10, Q11, Q12, Q13, Q14, Q15, Q16, Q17, Q18, Q19, Q20, Q21, Q22, Q23, Q24, Q25, Q26, Q27, Q28, Q29, Q30, Q31, Q32, Q33, Q34, Q35, Q36, Q37, Q38, Q39]), "depth" : 0.7 * mm, "offsetDistance" : 25 * mm});
        }
        {
            var Q0;
            {var subQ3=sQuery(id+"F4.wireOp",EDGE,"E95");Q0=makeQuery(id+"F4.imprint","IMPRINT",FACE,{"disambiguationData":[TD([[makeQuery(id+"F4.imprint","IMPRINT",EDGE,{"derivedFrom":subQ3}),1.0]])]});}
            var Q1;
            {var subQ5=sQuery(id+"F4.wireOp",EDGE,"E96");Q1=makeQuery(id+"F4.imprint","IMPRINT",FACE,{"disambiguationData":[TD([[makeQuery(id+"F4.imprint","IMPRINT",EDGE,{"derivedFrom":subQ5}),1.0]])]});}
            extrude(context, id + "F7", {"entities" : qUnion([Q0, Q1]), "depth" : 1.4 * mm, "offsetDistance" : 25 * mm});
        }
        {
            var Q0;
            Q0=makeQuery(id+"F5.opExtrude","SWEPT_EDGE",EDGE,{"disambiguationData":[OSD([sQuery(id+"F4.wireOp",EDGE,"E63"),sQuery(id+"F4.wireOp",EDGE,"E64")])]});
            var Q1;
            Q1=makeQuery(id+"F5.opExtrude","SWEPT_EDGE",EDGE,{"disambiguationData":[OSD([sQuery(id+"F4.wireOp",EDGE,"E62"),sQuery(id+"F4.wireOp",EDGE,"E63")])]});
            var Q2;
            Q2=makeQuery(id+"F5.opExtrude","SWEPT_EDGE",EDGE,{"disambiguationData":[OSD([sQuery(id+"F4.wireOp",EDGE,"E59"),sQuery(id+"F4.wireOp",EDGE,"E65")])]});
            var Q3;
            Q3=makeQuery(id+"F5.opExtrude","SWEPT_EDGE",EDGE,{"disambiguationData":[OSD([sQuery(id+"F4.wireOp",EDGE,"E65"),sQuery(id+"F4.wireOp",EDGE,"E66")])]});
            fillet(context, id + "F8", {"entities" : qUnion([Q0, Q1, Q2, Q3]), "tangentPropagation" : true, "radius" : 0.5 * mm, "defaultsChanged" : true, "vertexSettings" : [], "allowEdgeOverflow" : false});
        }
        {
            var Q0;
            Q0=makeQuery(id+"F6.opExtrude","SWEPT_EDGE",EDGE,{"disambiguationData":[OSD([sQuery(id+"F4.wireOp",EDGE,"E63"),sQuery(id+"F4.wireOp",EDGE,"E64")])]});
            var Q1;
            Q1=makeQuery(id+"F6.opExtrude","SWEPT_EDGE",EDGE,{"disambiguationData":[OSD([sQuery(id+"F4.wireOp",EDGE,"E62"),sQuery(id+"F4.wireOp",EDGE,"E63")])]});
            fillet(context, id + "F9", {"entities" : qUnion([Q0, Q1]), "tangentPropagation" : true, "radius" : 0.5 * mm, "defaultsChanged" : false, "vertexSettings" : [], "allowEdgeOverflow" : false});
        }
    });
